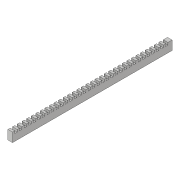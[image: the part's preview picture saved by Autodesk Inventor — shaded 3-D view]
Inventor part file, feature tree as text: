
AUTODESK INVENTOR PART (.ipt)
format: ipt  version: 2019 (Build 230136000, 136)  size: 311,296 bytes
history: native  units: in
note: dims shown in document units (in); Inventor stores cm internally (conversion verified against a paired STEP export)
features: extrude x3, sketch x3
ambient origin geometry x8: Origin, YZ Plane, XZ Plane, XY Plane, X Axis, Y Axis, Z Axis, Center Point
bodies: Solid1 (feature_tree)
feature tree (6):
  extrude  "Extrusion1"  Depth=1.5748in
  extrude  "Extrusion2"  Depth=1.5748in
  extrude  "Extrusion3"  Depth=0.3937in
  sketch  "Sketch1"  dims[d0=27.5591in d1=1.5748in]
  sketch  "Sketch2"  dims[d2=27.5591in d3=1.5748in]
  sketch  "Sketch3"  dims[d4=0.7874in d5=0.0in d6=0.3937in d7=0.3937in d8=0.3937in d9=0.3937in d10=0.3937in d11=0.3937in d12=0.3937in d13=0.3937in d14=0.3937in d15=0.3937in d16=0.3937in d17=0.3937in d18=0.3937in d19=0.3937in d20=0.3937in d21=0.3937in d22=0.3937in d23=0.3937in d24=0.3937in d25=0.3937in d26=0.3937in d27=0.3937in d28=0.3937in d29=0.3937in d30=0.3937in d31=0.3937in d32=0.3937in d33=0.3937in d34=0.3937in d35=0.3937in d36=0.3937in d37=0.3937in d38=0.3937in d39=0.3937in d40=0.3937in d41=0.3937in d42=0.3937in d43=0.3937in d44=0.3937in d45=27.5591in d46=1.5748in d47=0.0in d48=0.3937in d49=0.3937in d50=0.3937in d51=0.3937in d52=0.3937in d53=0.3937in d54=0.3937in d55=0.3937in d56=0.3937in d57=0.3937in d58=0.3937in d59=0.3937in d60=0.3937in d61=0.3937in d62=0.3937in d63=0.3937in d64=0.3937in d65=0.3937in d66=0.3937in d67=0.3937in d68=0.3937in d69=0.3937in d70=0.3937in d71=0.3937in d72=0.3937in d73=0.3937in d74=0.3937in d75=0.3937in d76=0.3937in d77=0.3937in d78=0.3937in d79=0.3937in d80=0.3937in d81=0.3937in d82=0.3937in d83=0.3937in d84=0.3937in d85=0.3937in d86=0.3937in d87=0.3937in d88=0.3937in d89=0.3937in d90=0.3937in d91=0.3937in d92=0.3937in d93=0.3937in d94=0.3937in d95=0.3937in d96=0.3937in d97=0.3937in d98=0.3937in d99=0.3937in d100=0.3937in d101=0.3937in d102=0.3937in d103=0.3937in d104=0.3937in d105=0.3937in d106=0.3937in d107=0.3937in d108=0.3937in d109=0.3937in d110=0.3937in d111=0.3937in d112=0.3937in d113=0.3937in d114=0.3937in d115=0.3937in d116=0.3937in d117=0.3937in d118=0.3937in d119=0.3937in d120=0.3937in d121=0.3937in d122=0.3937in d123=0.3937in d124=0.3937in d125=0.3937in d126=0.3937in d127=0.3937in d128=0.3937in d129=0.3937in d130=0.3937in d131=0.3937in d132=0.3937in d133=0.3937in d134=0.3937in d135=0.3937in d136=0.3937in d137=0.3937in d138=0.3937in d139=0.3937in d140=0.3937in d141=0.3937in d142=0.3937in d143=0.3937in d144=0.3937in d145=0.3937in d146=0.3937in d147=5.9055in d148=0.0in]
